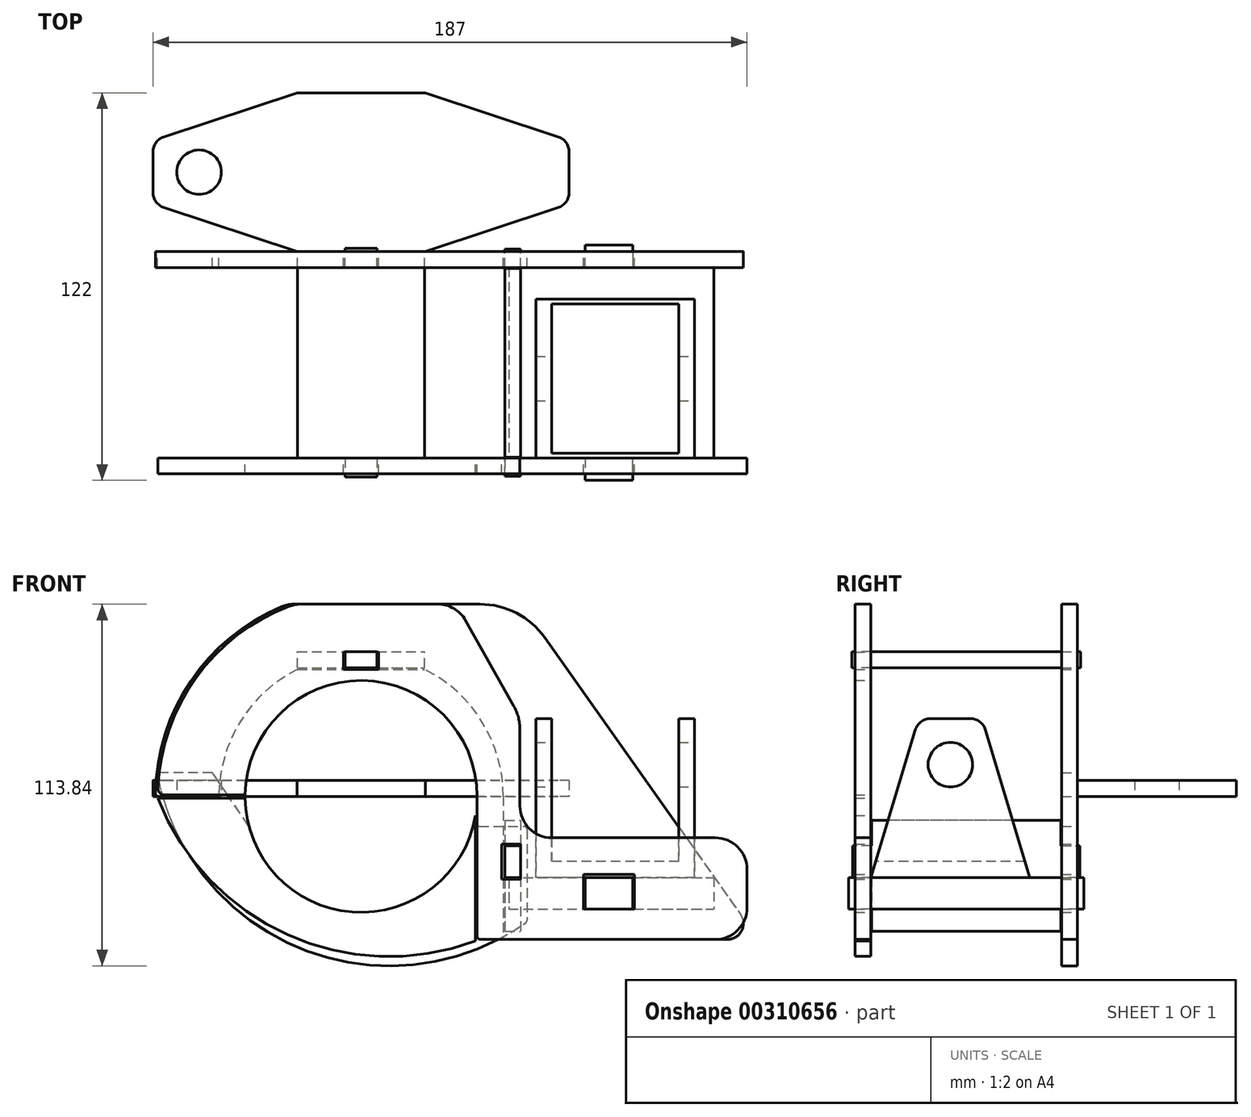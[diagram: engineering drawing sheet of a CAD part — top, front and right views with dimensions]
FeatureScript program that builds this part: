
annotation { "Feature Type Name" : "Feature", "Feature Type Description" : "" }
export const myFeature = defineFeature(function(context is Context, id is Id, definition is map)
    precondition{}
    {
        {
            var Q0;
            Q0=qCreatedBy(makeId("Front.planeOp"),FACE);
            var sketch = newSketch(context, id + "F0", { "sketchPlane" : qUnion([Q0])});
            skArc(sketch, "E0", {"start": v(44.75, 0) * mm, "mid": v(0, 44.75) * mm, "end": v(-44.75, 0) * mm, "construction": true});
            skLineSegment(sketch, "E1", {"start": v(-20, 40.03) * mm, "end": v(-5.5, 40.03) * mm});
            skLineSegment(sketch, "E2", {"start": v(-5.5, 40.03) * mm, "end": v(-5.5, 45.53) * mm});
            skLineSegment(sketch, "E3", {"start": v(-5.5, 45.53) * mm, "end": v(5.5, 45.53) * mm});
            skLineSegment(sketch, "E4", {"start": v(5.5, 45.53) * mm, "end": v(5.5, 40.03) * mm});
            skLineSegment(sketch, "E5", {"start": v(5.5, 40.03) * mm, "end": v(20, 40.03) * mm});
            skPoint(sketch, "E6", {"position": v(0, 45.53) * mm});
            skArc(sketch, "E7", {"start": v(-20, 40.03) * mm, "mid": v(-38.06, 23.53) * mm, "end": v(-44.75, 0) * mm});
            skArc(sketch, "E8", {"start": v(44.75, 0) * mm, "mid": v(38.06, 23.53) * mm, "end": v(20, 40.03) * mm});
            skArc(sketch, "E9.0", {"start": v(-24.92, 59.76) * mm, "mid": v(-53.6, 36.33) * mm, "end": v(-64.74, 1.02) * mm});
            skLineSegment(sketch, "E10", {"start": v(-63.74, 0) * mm, "end": v(-44.75, 0) * mm});
            skLineSegment(sketch, "E11", {"start": v(-21.07, 60.53) * mm, "end": v(37.4, 60.53) * mm});
            skLineSegment(sketch, "E12", {"start": v(44.75, 0) * mm, "end": v(44.75, -15) * mm});
            skLineSegment(sketch, "E13", {"start": v(44.75, -45) * mm, "end": v(115.34, -45) * mm});
            skArc(sketch, "E14", {"start": v(-36.5, 0) * mm, "mid": v(0, -36.5) * mm, "end": v(36.5, 0) * mm, "construction": true});
            skLineSegment(sketch, "E15", {"start": v(-44.75, 0) * mm, "end": v(-36.5, 0) * mm, "construction": true});
            skLineSegment(sketch, "E16", {"start": v(44.75, 0) * mm, "end": v(36.5, 0) * mm, "construction": true});
            skPoint(sketch, "E17", {"position": v(80, 10) * mm});
            skLineSegment(sketch, "E18", {"start": v(57.82, 49.97) * mm, "end": v(119.42, -37.11) * mm});
            skLineSegment(sketch, "E19.bottom", {"start": v(70, -24.5) * mm, "end": v(86, -24.5) * mm});
            skLineSegment(sketch, "E19.top", {"start": v(70, -35.5) * mm, "end": v(86, -35.5) * mm});
            skLineSegment(sketch, "E19.left", {"start": v(70, -24.5) * mm, "end": v(70, -35.5) * mm});
            skLineSegment(sketch, "E19.right", {"start": v(86, -24.5) * mm, "end": v(86, -35.5) * mm});
            skPoint(sketch, "E20.visualSharp", {"position": v(-22.99, 60.53) * mm});
            skArc(sketch, "E20.filletArc", {"start": v(-21.07, 60.53) * mm, "mid": v(-23.04, 60.34) * mm, "end": v(-24.92, 59.76) * mm});
            skPoint(sketch, "E21.visualSharp", {"position": v(50.35, 60.53) * mm});
            skArc(sketch, "E21.filletArc", {"start": v(57.82, 49.97) * mm, "mid": v(48.9, 57.73) * mm, "end": v(37.4, 60.53) * mm});
            skPoint(sketch, "E22.visualSharp", {"position": v(125, -45) * mm});
            skArc(sketch, "E22.filletArc", {"start": v(115.34, -45) * mm, "mid": v(119.78, -42.3) * mm, "end": v(119.42, -37.11) * mm});
            skLineSegment(sketch, "E23", {"start": v(44.75, -15) * mm, "end": v(50.25, -15) * mm});
            skLineSegment(sketch, "E24", {"start": v(50.25, -15) * mm, "end": v(50.25, -26) * mm});
            skLineSegment(sketch, "E25", {"start": v(50.25, -26) * mm, "end": v(44.75, -26) * mm});
            skLineSegment(sketch, "E26.trimOffspring", {"start": v(44.75, -26) * mm, "end": v(44.75, -45) * mm});
            skPoint(sketch, "E27.visualSharp", {"position": v(-64.75, 0) * mm});
            skArc(sketch, "E27.filletArc", {"start": v(-64.74, 1.02) * mm, "mid": v(-64.45, 0.3) * mm, "end": v(-63.74, 0) * mm});
            skSolve(sketch);
        }
        {
            var Q0;
            Q0=qSketchRegion(id+"F0",true);
            var Q1;
            Q1=qConstructionFilter(qBodyType(qCreatedBy(id+"F0",EDGE),BodyType.WIRE),ConstructionObject.NO);
            extrude(context, id + "F1", {"entities" : qUnion([Q0]), "surfaceEntities" : qUnion([Q1]), "depth" : 5 * mm});
        }
        {
            var Q0;
            Q0=qCreatedBy(makeId("Front.planeOp"),FACE);
            var sketch = newSketch(context, id + "F2", { "sketchPlane" : qUnion([Q0])});
            skArc(sketch, "E28", {"start": v(-35.15, -9.84) * mm, "mid": v(-0.7, -36.5) * mm, "end": v(34.75, -11.18) * mm});
            skLineSegment(sketch, "E29", {"start": v(-35.26, -9.45) * mm, "end": v(0, 0) * mm, "construction": true});
            skLineSegment(sketch, "E30", {"start": v(35.26, -9.45) * mm, "end": v(0, 0) * mm, "construction": true});
            skLineSegment(sketch, "E31", {"start": v(-35.5, -9.1) * mm, "end": v(-46.81, 7.5) * mm});
            skLineSegment(sketch, "E32", {"start": v(-46.81, 7.5) * mm, "end": v(-63.1, 7.5) * mm});
            skLineSegment(sketch, "E33", {"start": v(37.13, -9.45) * mm, "end": v(51.25, -9.45) * mm});
            skLineSegment(sketch, "E34", {"start": v(52.25, -10.45) * mm, "end": v(52.25, -38.93) * mm});
            skArc(sketch, "E35", {"start": v(-64.08, 6.3) * mm, "mid": v(-18.57, -48.04) * mm, "end": v(51.83, -39.75) * mm});
            skPoint(sketch, "E36.visualSharp", {"position": v(-35.26, -9.45) * mm});
            skArc(sketch, "E36.filletArc", {"start": v(-35.15, -9.84) * mm, "mid": v(-35.3, -9.46) * mm, "end": v(-35.5, -9.1) * mm});
            skPoint(sketch, "E37.visualSharp", {"position": v(35.26, -9.45) * mm});
            skArc(sketch, "E37.filletArc", {"start": v(37.13, -9.45) * mm, "mid": v(35.65, -9.93) * mm, "end": v(34.75, -11.18) * mm});
            skPoint(sketch, "E38.visualSharp", {"position": v(-64.31, 7.5) * mm});
            skArc(sketch, "E38.filletArc", {"start": v(-63.1, 7.5) * mm, "mid": v(-63.87, 7.13) * mm, "end": v(-64.08, 6.3) * mm});
            skPoint(sketch, "E39.visualSharp", {"position": v(52.25, -39.45) * mm});
            skArc(sketch, "E39.filletArc", {"start": v(51.83, -39.75) * mm, "mid": v(52.14, -39.4) * mm, "end": v(52.25, -38.93) * mm});
            skPoint(sketch, "E40.visualSharp", {"position": v(52.25, -9.45) * mm});
            skArc(sketch, "E40.filletArc", {"start": v(52.25, -10.45) * mm, "mid": v(51.96, -9.74) * mm, "end": v(51.25, -9.45) * mm});
            skSolve(sketch);
        }
        {
            var Q0;
            Q0=qSketchRegion(id+"F2",true);
            extrude(context, id + "F3", {"entities" : qUnion([Q0]), "depth" : 5 * mm});
        }
        {
            var Q0;
            Q0=makeQuery(id+"F1.opExtrude","SWEPT_FACE",FACE,{"disambiguationData":[OSD([sQuery(id+"F0.wireOp",EDGE,"E19.top")])]});
            var sketch = newSketch(context, id + "F4", { "sketchPlane" : qUnion([Q0])});
            skLineSegment(sketch, "E41.bottom", {"start": v(46.5, -5) * mm, "end": v(111, -5) * mm});
            skLineSegment(sketch, "E41.top", {"start": v(46.5, -65) * mm, "end": v(111, -65) * mm});
            skLineSegment(sketch, "E41.left", {"start": v(46.5, -5) * mm, "end": v(46.5, -65) * mm});
            skLineSegment(sketch, "E41.right", {"start": v(111, -5) * mm, "end": v(111, -65) * mm});
            skLineSegment(sketch, "E42", {"start": v(70.5, -5) * mm, "end": v(70.5, 2) * mm});
            skLineSegment(sketch, "E43", {"start": v(70.5, 2) * mm, "end": v(85.5, 2) * mm});
            skLineSegment(sketch, "E44", {"start": v(85.5, 2) * mm, "end": v(85.5, -5) * mm});
            skLineSegment(sketch, "E45", {"start": v(70.5, -65) * mm, "end": v(70.5, -72) * mm});
            skLineSegment(sketch, "E46", {"start": v(70.5, -72) * mm, "end": v(85.5, -72) * mm});
            skLineSegment(sketch, "E47", {"start": v(85.5, -72) * mm, "end": v(85.5, -65) * mm});
            skSolve(sketch);
        }
        {
            var Q0;
            Q0=qSketchRegion(id+"F4",true);
            extrude(context, id + "F5", {"entities" : qUnion([Q0]), "depth" : 10 * mm});
        }
        {
            var Q0;
            {var subQ0=sQuery(id+"F4.wireOp",EDGE,"E41.top");Q0=makeQuery(id+"F5.opExtrude","SWEPT_FACE",FACE,{"disambiguationData":[OSD([subQ0]),TDD([makeQuery(id+"F4.imprint","IMPRINT",EDGE,{"disambiguationData":[TD([[makeQuery(id+"F4.imprint","INTERSECT",VERTEX,{"derivedFrom":[subQ0,sQuery(id+"F4.wireOp",EDGE,"E41.left")]}),-1.0]])],"derivedFrom":subQ0})])]});}
            var sketch = newSketch(context, id + "F6", { "sketchPlane" : qUnion([Q0])});
            skLineSegment(sketch, "E48", {"start": v(60, 24.5) * mm, "end": v(60, -20.5) * mm});
            skLineSegment(sketch, "E49", {"start": v(60, -20.5) * mm, "end": v(100, -20.5) * mm});
            skLineSegment(sketch, "E50", {"start": v(100, -20.5) * mm, "end": v(100, 24.5) * mm});
            skLineSegment(sketch, "E51", {"start": v(100, 24.5) * mm, "end": v(105, 24.5) * mm});
            skLineSegment(sketch, "E52", {"start": v(105, 24.5) * mm, "end": v(105, -25.5) * mm});
            skLineSegment(sketch, "E53", {"start": v(105, -25.5) * mm, "end": v(55, -25.5) * mm});
            skLineSegment(sketch, "E54", {"start": v(55, -25.5) * mm, "end": v(55, 24.5) * mm});
            skLineSegment(sketch, "E55", {"start": v(55, 24.5) * mm, "end": v(60, 24.5) * mm});
            skSolve(sketch);
        }
        {
            var Q0;
            Q0=qSketchRegion(id+"F6",true);
            extrude(context, id + "F7", {"entities" : qUnion([Q0]), "oppositeDirection" : true, "depth" : 50 * mm});
        }
        {
            var Q0;
            Q0=makeQuery(id+"F7.opExtrude","SWEPT_FACE",FACE,{"disambiguationData":[OSD([sQuery(id+"F6.wireOp",EDGE,"E52")])]});
            var sketch = newSketch(context, id + "F8", { "sketchPlane" : qUnion([Q0])});
            skCircle(sketch, "E56", {"center": v(-40, 10) * mm, "radius": 7 * mm});
            skLineSegment(sketch, "E57", {"start": v(-46.28, 24.5) * mm, "end": v(-33.72, 24.5) * mm});
            skPoint(sketch, "E58", {"position": v(-40, 24.5) * mm});
            skLineSegment(sketch, "E59", {"start": v(-65, -25.5) * mm, "end": v(-51.07, 20.94) * mm});
            skLineSegment(sketch, "E60", {"start": v(-28.93, 20.94) * mm, "end": v(-15, -25.5) * mm});
            skPoint(sketch, "E61.visualSharp", {"position": v(-50, 24.5) * mm});
            skArc(sketch, "E61.filletArc", {"start": v(-46.28, 24.5) * mm, "mid": v(-49.26, 23.51) * mm, "end": v(-51.07, 20.94) * mm});
            skPoint(sketch, "E62.visualSharp", {"position": v(-30, 24.5) * mm});
            skArc(sketch, "E62.filletArc", {"start": v(-28.93, 20.94) * mm, "mid": v(-30.74, 23.51) * mm, "end": v(-33.72, 24.5) * mm});
            skLineSegment(sketch, "E63", {"start": v(-46.28, 24.5) * mm, "end": v(-65, 24.5) * mm});
            skLineSegment(sketch, "E64", {"start": v(-65, 24.5) * mm, "end": v(-65, -25.5) * mm});
            skLineSegment(sketch, "E65", {"start": v(-33.72, 24.5) * mm, "end": v(-15, 24.5) * mm});
            skLineSegment(sketch, "E66", {"start": v(-15, 24.5) * mm, "end": v(-15, -25.5) * mm});
            skSolve(sketch);
        }
        {
            var Q0;
            Q0=qSketchRegion(id+"F8",true);
            extrude(context, id + "F9", {"entities" : qUnion([Q0]), "operationType" : NewBodyOperationType.REMOVE, "oppositeDirection" : true, "depth" : 602 * mm});
        }
        {
            var Q0;
            {var subQ0=sQuery(id+"F4.wireOp",EDGE,"E41.top");Q0=makeQuery(id+"F5.opExtrude","SWEPT_FACE",FACE,{"disambiguationData":[OSD([subQ0]),TDD([makeQuery(id+"F4.imprint","IMPRINT",EDGE,{"disambiguationData":[TD([[makeQuery(id+"F4.imprint","INTERSECT",VERTEX,{"derivedFrom":[subQ0,sQuery(id+"F4.wireOp",EDGE,"E41.right")]}),1.0]])],"derivedFrom":subQ0})])]});}
            var sketch = newSketch(context, id + "F10", { "sketchPlane" : qUnion([Q0])});
            skArc(sketch, "E67", {"start": v(36.5, 0) * mm, "mid": v(0.25, 36.5) * mm, "end": v(-36.5, 0.5) * mm});
            skLineSegment(sketch, "E68", {"start": v(-36.5, 0.5) * mm, "end": v(-61.95, 0.5) * mm});
            skArc(sketch, "E69", {"start": v(-22.56, 59.9) * mm, "mid": v(-51.88, 37.47) * mm, "end": v(-63.95, 2.58) * mm});
            skLineSegment(sketch, "E70", {"start": v(-19.04, 60.53) * mm, "end": v(24.15, 60.53) * mm});
            skPoint(sketch, "E71.orphan", {"position": v(0, 64) * mm});
            skLineSegment(sketch, "E72", {"start": v(50, 21.07) * mm, "end": v(50, 0.02) * mm});
            skLineSegment(sketch, "E73", {"start": v(36.5, 0) * mm, "end": v(36.5, -44) * mm});
            skLineSegment(sketch, "E74", {"start": v(37.5, -45) * mm, "end": v(111.5, -45) * mm});
            skLineSegment(sketch, "E75", {"start": v(121.5, -35) * mm, "end": v(121.5, -23) * mm});
            skLineSegment(sketch, "E76", {"start": v(111.5, -13) * mm, "end": v(60, -13) * mm});
            skLineSegment(sketch, "E77", {"start": v(50, -3) * mm, "end": v(50, 0.02) * mm});
            skLineSegment(sketch, "E78.bottom", {"start": v(70, -24.5) * mm, "end": v(86, -24.5) * mm});
            skLineSegment(sketch, "E78.top", {"start": v(70, -35.5) * mm, "end": v(86, -35.5) * mm});
            skLineSegment(sketch, "E78.left", {"start": v(70, -24.5) * mm, "end": v(70, -35.5) * mm});
            skLineSegment(sketch, "E78.right", {"start": v(86, -24.5) * mm, "end": v(86, -35.5) * mm});
            skPoint(sketch, "E79.visualSharp", {"position": v(-20.78, 60.53) * mm});
            skArc(sketch, "E79.filletArc", {"start": v(-19.04, 60.53) * mm, "mid": v(-20.83, 60.37) * mm, "end": v(-22.56, 59.9) * mm});
            skPoint(sketch, "E80.visualSharp", {"position": v(-64, 0.5) * mm});
            skArc(sketch, "E80.filletArc", {"start": v(-63.95, 2.58) * mm, "mid": v(-63.4, 1.11) * mm, "end": v(-61.95, 0.5) * mm});
            skPoint(sketch, "E81.visualSharp", {"position": v(50, 60.53) * mm});
            skPoint(sketch, "E82.visualSharp", {"position": v(50, -13) * mm});
            skArc(sketch, "E82.filletArc", {"start": v(50, -3) * mm, "mid": v(52.93, -10.07) * mm, "end": v(60, -13) * mm});
            skPoint(sketch, "E83.visualSharp", {"position": v(36.5, -45) * mm});
            skArc(sketch, "E83.filletArc", {"start": v(36.5, -44) * mm, "mid": v(36.8, -44.7) * mm, "end": v(37.5, -45) * mm});
            skPoint(sketch, "E84.visualSharp", {"position": v(121.5, -45) * mm});
            skArc(sketch, "E84.filletArc", {"start": v(111.5, -45) * mm, "mid": v(118.57, -42.07) * mm, "end": v(121.5, -35) * mm});
            skPoint(sketch, "E85.visualSharp", {"position": v(121.5, -13) * mm});
            skArc(sketch, "E85.filletArc", {"start": v(121.5, -23) * mm, "mid": v(118.57, -15.93) * mm, "end": v(111.5, -13) * mm});
            skLineSegment(sketch, "E86", {"start": v(32.87, 55.44) * mm, "end": v(48.07, 28.43) * mm});
            skPoint(sketch, "E87.visualSharp", {"position": v(50, 25) * mm});
            skArc(sketch, "E87.filletArc", {"start": v(50, 21.07) * mm, "mid": v(49.5, 24.87) * mm, "end": v(48.07, 28.43) * mm});
            skPoint(sketch, "E88.visualSharp", {"position": v(30, 60.53) * mm});
            skArc(sketch, "E88.filletArc", {"start": v(32.87, 55.44) * mm, "mid": v(29.2, 59.16) * mm, "end": v(24.15, 60.53) * mm});
            skArc(sketch, "E89", {"start": v(-36.5, -0.5) * mm, "mid": v(-2.77, -36.4) * mm, "end": v(36, -6.02) * mm});
            skLineSegment(sketch, "E90", {"start": v(36, -6.02) * mm, "end": v(36, -45.5) * mm});
            skLineSegment(sketch, "E91", {"start": v(-64, -0.5) * mm, "end": v(-36.5, -0.5) * mm});
            skArc(sketch, "E92", {"start": v(-64, -0.5) * mm, "mid": v(-23.22, -43.5) * mm, "end": v(36, -45.5) * mm});
            skLineSegment(sketch, "E93.bottom", {"start": v(-5.5, 40) * mm, "end": v(5.5, 40) * mm});
            skLineSegment(sketch, "E93.top", {"start": v(-5.5, 45.5) * mm, "end": v(5.5, 45.5) * mm});
            skLineSegment(sketch, "E93.left", {"start": v(-5.5, 40) * mm, "end": v(-5.5, 45.5) * mm});
            skLineSegment(sketch, "E93.right", {"start": v(5.5, 40) * mm, "end": v(5.5, 45.5) * mm});
            skPoint(sketch, "E94", {"position": v(0, 40) * mm});
            skLineSegment(sketch, "E95.bottom", {"start": v(44.25, -15) * mm, "end": v(50.25, -15) * mm});
            skLineSegment(sketch, "E95.top", {"start": v(44.25, -26) * mm, "end": v(50.25, -26) * mm});
            skLineSegment(sketch, "E95.left", {"start": v(44.25, -15) * mm, "end": v(44.25, -26) * mm});
            skLineSegment(sketch, "E95.right", {"start": v(50.25, -15) * mm, "end": v(50.25, -26) * mm});
            skSolve(sketch);
        }
        {
            var Q0;
            Q0=qSketchRegion(id+"F10",true);
            extrude(context, id + "F11", {"entities" : qUnion([Q0]), "depth" : 5 * mm});
        }
        {
            var Q0;
            Q0=makeQuery(id+"F1.opExtrude","SWEPT_FACE",FACE,{"disambiguationData":[OSD([sQuery(id+"F0.wireOp",EDGE,"E3")])]});
            var sketch = newSketch(context, id + "F12", { "sketchPlane" : qUnion([Q0])});
            skLineSegment(sketch, "E96.bottom", {"start": v(-20, 5) * mm, "end": v(20, 5) * mm});
            skLineSegment(sketch, "E96.top", {"start": v(-20, 65) * mm, "end": v(20, 65) * mm});
            skLineSegment(sketch, "E96.left", {"start": v(-20, 5) * mm, "end": v(-20, 65) * mm});
            skLineSegment(sketch, "E96.right", {"start": v(20, 5) * mm, "end": v(20, 65) * mm});
            skLineSegment(sketch, "E97.bottom", {"start": v(-5, 5) * mm, "end": v(5, 5) * mm});
            skLineSegment(sketch, "E97.top", {"start": v(-5, -1) * mm, "end": v(5, -1) * mm});
            skLineSegment(sketch, "E97.left", {"start": v(-5, 5) * mm, "end": v(-5, -1) * mm});
            skLineSegment(sketch, "E97.right", {"start": v(5, 5) * mm, "end": v(5, -1) * mm});
            skLineSegment(sketch, "E98.bottom", {"start": v(-5, 65) * mm, "end": v(5, 65) * mm});
            skLineSegment(sketch, "E98.top", {"start": v(-5, 71) * mm, "end": v(5, 71) * mm});
            skLineSegment(sketch, "E98.left", {"start": v(-5, 65) * mm, "end": v(-5, 71) * mm});
            skLineSegment(sketch, "E98.right", {"start": v(5, 65) * mm, "end": v(5, 71) * mm});
            skSolve(sketch);
        }
        {
            var Q0;
            Q0=qSketchRegion(id+"F12",true);
            extrude(context, id + "F13", {"entities" : qUnion([Q0]), "depth" : 5 * mm});
        }
        {
            var Q0;
            Q0=makeQuery(id+"F1.opExtrude","SWEPT_FACE",FACE,{"disambiguationData":[OSD([sQuery(id+"F0.wireOp",EDGE,"E24")])]});
            var sketch = newSketch(context, id + "F14", { "sketchPlane" : qUnion([Q0])});
            skLineSegment(sketch, "E99.bottom", {"start": v(5.25, -7.5) * mm, "end": v(64.75, -7.5) * mm});
            skLineSegment(sketch, "E99.top", {"start": v(5.25, -42.5) * mm, "end": v(64.75, -42.5) * mm});
            skLineSegment(sketch, "E99.left", {"start": v(5.25, -7.5) * mm, "end": v(5.25, -42.5) * mm});
            skLineSegment(sketch, "E99.right", {"start": v(64.75, -7.5) * mm, "end": v(64.75, -42.5) * mm});
            skLineSegment(sketch, "E100.bottom", {"start": v(5.25, -15.5) * mm, "end": v(-0.75, -15.5) * mm});
            skLineSegment(sketch, "E100.top", {"start": v(5.25, -25.5) * mm, "end": v(-0.75, -25.5) * mm});
            skLineSegment(sketch, "E100.left", {"start": v(5.25, -15.5) * mm, "end": v(5.25, -25.5) * mm});
            skLineSegment(sketch, "E100.right", {"start": v(-0.75, -15.5) * mm, "end": v(-0.75, -25.5) * mm});
            skLineSegment(sketch, "E101.bottom", {"start": v(64.75, -15.5) * mm, "end": v(70.75, -15.5) * mm});
            skLineSegment(sketch, "E101.left", {"start": v(64.75, -15.5) * mm, "end": v(64.75, -26) * mm});
            skLineSegment(sketch, "E101.right", {"start": v(70.75, -15.5) * mm, "end": v(70.75, -25.5) * mm});
            skLineSegment(sketch, "E102", {"start": v(70.75, -25.5) * mm, "end": v(64.75, -25.5) * mm});
            skSolve(sketch);
        }
        {
            var Q0;
            Q0=qSketchRegion(id+"F14",true);
            extrude(context, id + "F15", {"entities" : qUnion([Q0]), "depth" : 5 * mm});
        }
        {
            var Q0;
            Q0=qCreatedBy(makeId("Top.planeOp"),FACE);
            var sketch = newSketch(context, id + "F16", { "sketchPlane" : qUnion([Q0])});
            skLineSegment(sketch, "E103.bottom", {"start": v(-20.2, 0) * mm, "end": v(20.2, 0) * mm});
            skLineSegment(sketch, "E103.top", {"start": v(-20.2, 50) * mm, "end": v(20.2, 50) * mm});
            skLineSegment(sketch, "E103.left", {"start": v(-20.2, 0) * mm, "end": v(-20.2, 50) * mm});
            skLineSegment(sketch, "E103.right", {"start": v(20.2, 0) * mm, "end": v(20.2, 50) * mm});
            skCircle(sketch, "E104", {"center": v(-51, 25) * mm, "radius": 7 * mm});
            skLineSegment(sketch, "E105", {"start": v(-20.2, 0) * mm, "end": v(-62.07, 13.86) * mm});
            skLineSegment(sketch, "E106", {"start": v(-65.5, 18.61) * mm, "end": v(-65.5, 31.39) * mm});
            skLineSegment(sketch, "E107", {"start": v(-62.07, 36.14) * mm, "end": v(-20.2, 50) * mm});
            skLineSegment(sketch, "E108", {"start": v(20.2, 0) * mm, "end": v(62.07, 13.86) * mm});
            skLineSegment(sketch, "E109", {"start": v(65.5, 18.61) * mm, "end": v(65.5, 31.39) * mm});
            skLineSegment(sketch, "E110", {"start": v(62.07, 36.14) * mm, "end": v(20.2, 50) * mm});
            skPoint(sketch, "E111", {"position": v(-65.5, 25) * mm});
            skPoint(sketch, "E112", {"position": v(65.5, 25) * mm});
            skPoint(sketch, "E113.visualSharp", {"position": v(-65.5, 15) * mm});
            skArc(sketch, "E113.filletArc", {"start": v(-65.5, 18.61) * mm, "mid": v(-64.55, 15.68) * mm, "end": v(-62.07, 13.86) * mm});
            skPoint(sketch, "E114.visualSharp", {"position": v(-65.5, 35) * mm});
            skArc(sketch, "E114.filletArc", {"start": v(-62.07, 36.14) * mm, "mid": v(-64.55, 34.32) * mm, "end": v(-65.5, 31.39) * mm});
            skPoint(sketch, "E115.visualSharp", {"position": v(65.5, 35) * mm});
            skArc(sketch, "E115.filletArc", {"start": v(65.5, 31.39) * mm, "mid": v(64.55, 34.32) * mm, "end": v(62.07, 36.14) * mm});
            skPoint(sketch, "E116.visualSharp", {"position": v(65.5, 15) * mm});
            skArc(sketch, "E116.filletArc", {"start": v(62.07, 13.86) * mm, "mid": v(64.55, 15.68) * mm, "end": v(65.5, 18.61) * mm});
            skSolve(sketch);
        }
        {
            var Q0;
            Q0 = qSketchRegion(id + "F16", true);
            extrude(context, id + "F17", {"entities" : qUnion([Q0]), "depth" : 5 * mm});
        }
    });
